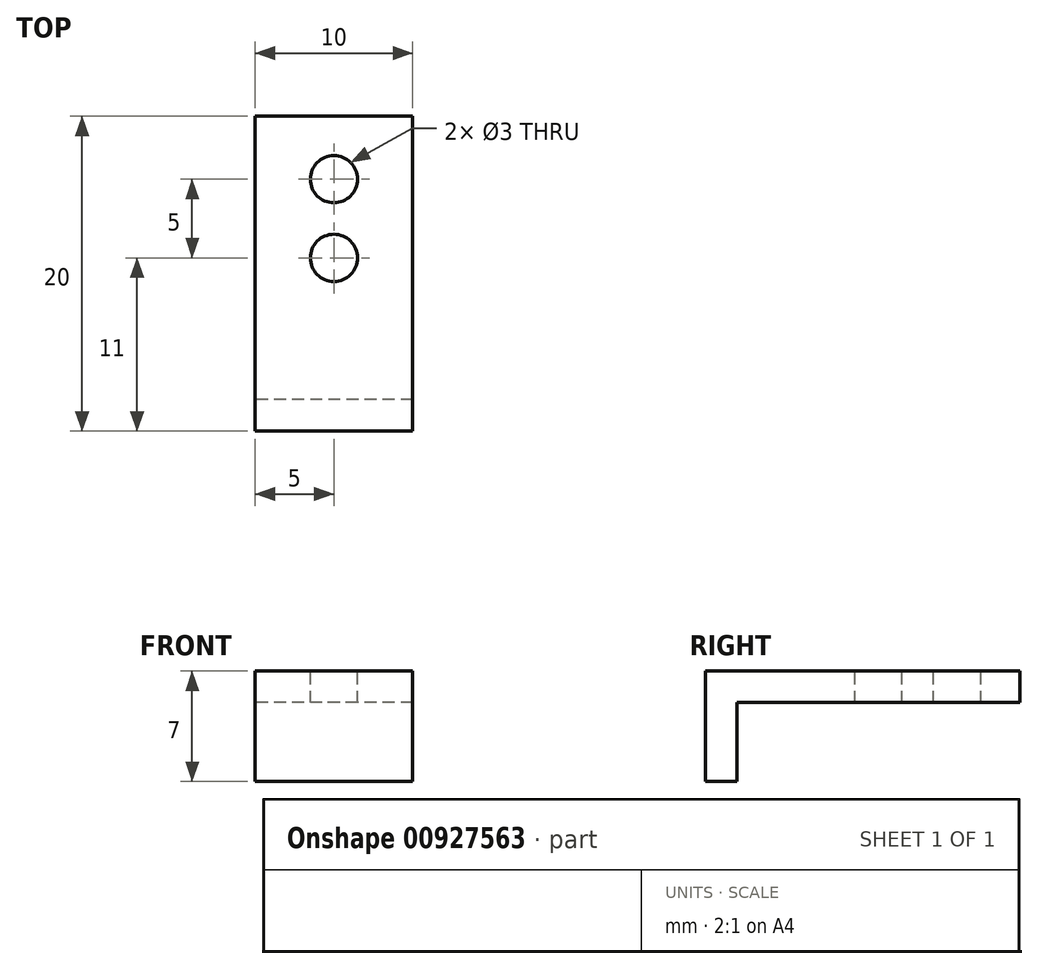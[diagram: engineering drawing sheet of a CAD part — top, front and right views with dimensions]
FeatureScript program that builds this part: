
annotation { "Feature Type Name" : "Feature", "Feature Type Description" : "" }
export const myFeature = defineFeature(function(context is Context, id is Id, definition is map)
    precondition{}
    {
        {
            var Q0;
            Q0=qCreatedBy(makeId("Right.planeOp"),FACE);
            var sketch = newSketch(context, id + "F0", { "sketchPlane" : qUnion([Q0])});
            skLineSegment(sketch, "E0", {"start": v(0, 0) * mm, "end": v(20, 0) * mm});
            skLineSegment(sketch, "E1", {"start": v(0, 0) * mm, "end": v(0, -7) * mm});
            skLineSegment(sketch, "E2.0", {"start": v(2, -2) * mm, "end": v(20, -2) * mm});
            skLineSegment(sketch, "E2.1", {"start": v(2, -2) * mm, "end": v(2, -7) * mm});
            skLineSegment(sketch, "E3", {"start": v(2, -7) * mm, "end": v(0, -7) * mm});
            skLineSegment(sketch, "E4", {"start": v(20, -2) * mm, "end": v(20, 0) * mm});
            skSolve(sketch);
        }
        {
            var Q0;
            Q0 = qSketchRegion(id + "F0", true);
            extrude(context, id + "F1", {"entities" : qUnion([Q0]), "depth" : 10 * mm, "offsetDistance" : 25 * mm});
        }
        {
            var Q0;
            Q0=makeQuery(id+"F1.opExtrude","SWEPT_FACE",FACE,{"disambiguationData":[OSD([sQuery(id+"F0.wireOp",EDGE,"E0")])]});
            var sketch = newSketch(context, id + "F2", { "sketchPlane" : qUnion([Q0])});
            skCircle(sketch, "E5", {"center": v(5, 16) * mm, "radius": 1.5 * mm});
            skCircle(sketch, "E6", {"center": v(5, 11) * mm, "radius": 1.5 * mm});
            skSolve(sketch);
        }
        {
            var Q0;
            Q0 = qSketchRegion(id + "F2", true);
            extrude(context, id + "F3", {"entities" : qUnion([Q0]), "operationType" : NewBodyOperationType.REMOVE, "oppositeDirection" : true, "depth" : 25 * mm, "offsetDistance" : 25 * mm});
        }
    });
